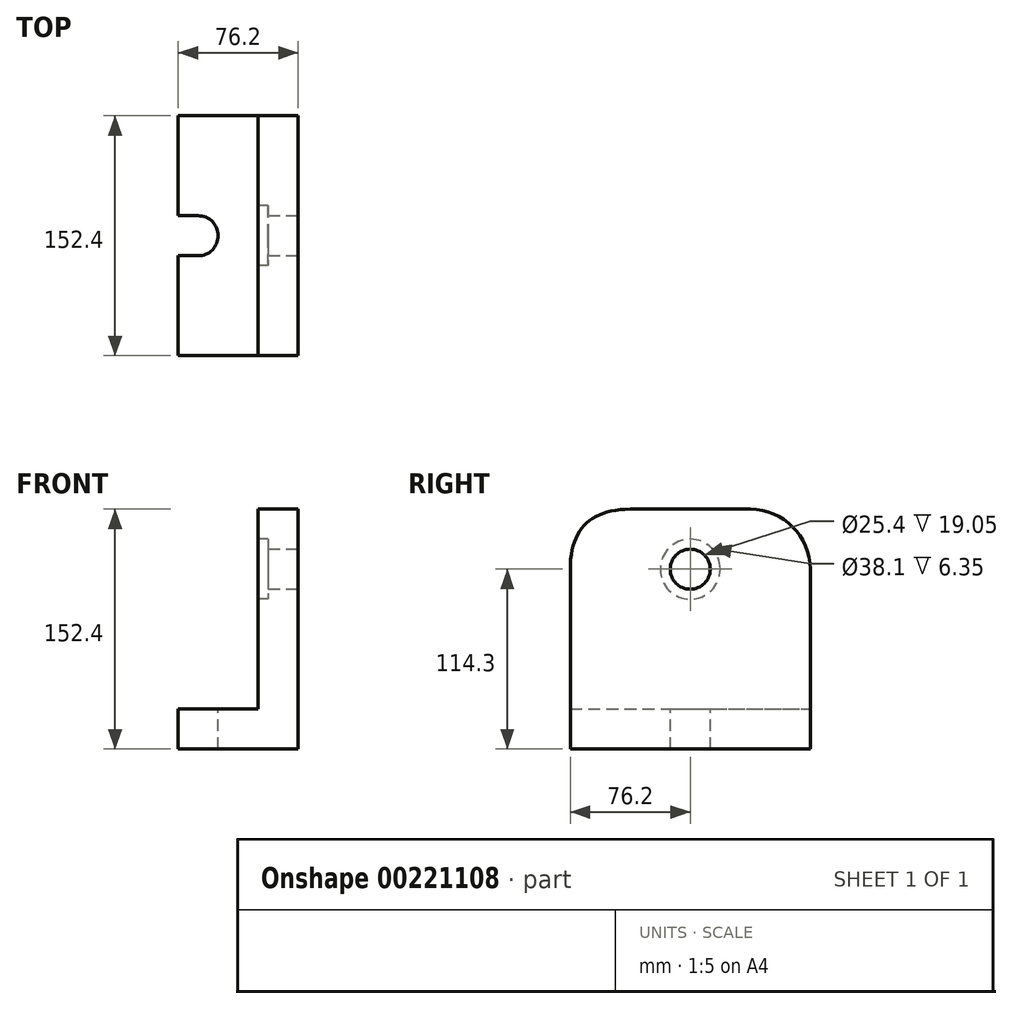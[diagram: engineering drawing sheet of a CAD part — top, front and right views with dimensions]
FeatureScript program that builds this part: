
annotation { "Feature Type Name" : "Feature", "Feature Type Description" : "" }
export const myFeature = defineFeature(function(context is Context, id is Id, definition is map)
    precondition{}
    {
        {
            var Q0;
            Q0=qCreatedBy(makeId("Front.planeOp"),FACE);
            var sketch = newSketch(context, id + "F0", { "sketchPlane" : qUnion([Q0])});
            skLineSegment(sketch, "E0", {"start": v(0, 0) * mm, "end": v(-76.2, 0) * mm});
            skLineSegment(sketch, "E1", {"start": v(0, 0) * mm, "end": v(0, 152.4) * mm});
            skLineSegment(sketch, "E2", {"start": v(-76.2, 0) * mm, "end": v(-76.2, 25.4) * mm});
            skLineSegment(sketch, "E3", {"start": v(-76.2, 25.4) * mm, "end": v(-25.4, 25.4) * mm});
            skLineSegment(sketch, "E4", {"start": v(-25.4, 25.4) * mm, "end": v(-25.4, 152.4) * mm});
            skLineSegment(sketch, "E5", {"start": v(-25.4, 152.4) * mm, "end": v(0, 152.4) * mm});
            skSolve(sketch);
        }
        {
            var Q0;
            Q0=makeQuery(id+"F0.imprint","IMPRINT",FACE,{"disambiguationData":[TD([[makeQuery(id+"F0.imprint","IMPRINT",EDGE,{"derivedFrom":sQuery(id+"F0.wireOp",EDGE,"E0")}),-1.0]])]});
            extrude(context, id + "F1", {"entities" : qUnion([Q0]), "endBound" : BoundingType.SYMMETRIC, "depth" : 152.4 * mm});
        }
        {
            var Q0;
            Q0=makeQuery(id+"F1.opExtrude","SWEPT_FACE",FACE,{"disambiguationData":[OSD([sQuery(id+"F0.wireOp",EDGE,"E1")])]});
            var sketch = newSketch(context, id + "F2", { "sketchPlane" : qUnion([Q0])});
            skCircle(sketch, "E6", {"center": v(0, 114.3) * mm, "radius": 12.7 * mm});
            skPoint(sketch, "E6.centerSnap0", {"position": v(0, 152.4) * mm});
            skSolve(sketch);
        }
        {
            var Q0;
            Q0=makeQuery(id+"F2.imprint","IMPRINT",FACE,{"disambiguationData":[TD([[makeQuery(id+"F2.imprint","IMPRINT",EDGE,{"derivedFrom":sQuery(id+"F2.wireOp",EDGE,"E6")}),1.0]])]});
            extrude(context, id + "F3", {"entities" : qUnion([Q0]), "operationType" : NewBodyOperationType.REMOVE, "oppositeDirection" : true, "depth" : 38.1 * mm});
        }
        {
            var Q0;
            Q0=makeQuery(id+"F1.opExtrude","SWEPT_FACE",FACE,{"disambiguationData":[OSD([sQuery(id+"F0.wireOp",EDGE,"E3")])]});
            var sketch = newSketch(context, id + "F4", { "sketchPlane" : qUnion([Q0])});
            skLineSegment(sketch, "E7", {"start": v(-76.2, 12.7) * mm, "end": v(-63.5, 12.7) * mm});
            skLineSegment(sketch, "E8", {"start": v(-76.2, -12.7) * mm, "end": v(-63.5, -12.7) * mm});
            skArc(sketch, "E9", {"start": v(-63.5, -12.7) * mm, "mid": v(-50.8, 0) * mm, "end": v(-63.5, 12.7) * mm});
            skSolve(sketch);
        }
        {
            var Q0;
            {var subQ0=sQuery(id+"F4.wireOp",EDGE,"E7");Q0=makeQuery(id+"F4.imprint","IMPRINT",FACE,{"disambiguationData":[TD([[makeQuery(id+"F4.imprint","IMPRINT",EDGE,{"derivedFrom":subQ0}),-1.0]])]});}
            extrude(context, id + "F5", {"entities" : qUnion([Q0]), "operationType" : NewBodyOperationType.REMOVE, "oppositeDirection" : true, "depth" : 25.4 * mm});
        }
        {
            var Q0;
            Q0=makeQuery(id+"F1.opExtrude","CAP_EDGE",EDGE,{"disambiguationData":[OSD([sQuery(id+"F0.wireOp",EDGE,"E5")])],"isStart":false});
            fillet(context, id + "F6", {"entities" : qUnion([Q0]), "radius" : 38.1 * mm, "tangentPropagation" : true, "rho" : 0.5, "crossSection" : FilletCrossSection.CONIC, "allowEdgeOverflow" : false});
        }
        {
            var Q0;
            Q0=makeQuery(id+"F1.opExtrude","CAP_EDGE",EDGE,{"disambiguationData":[OSD([sQuery(id+"F0.wireOp",EDGE,"E5")])],"isStart":true});
            fillet(context, id + "F7", {"entities" : qUnion([Q0]), "radius" : 38.1 * mm, "tangentPropagation" : true, "allowEdgeOverflow" : false});
        }
        {
            var Q0;
            Q0=makeQuery(id+"F1.opExtrude","SWEPT_FACE",FACE,{"disambiguationData":[OSD([sQuery(id+"F0.wireOp",EDGE,"E4")])]});
            var sketch = newSketch(context, id + "F8", { "sketchPlane" : qUnion([Q0])});
            skCircle(sketch, "E10", {"center": v(0, 114.3) * mm, "radius": 19.05 * mm});
            skSolve(sketch);
        }
        {
            var Q0;
            Q0=makeQuery(id+"F8.imprint","IMPRINT",FACE,{"disambiguationData":[TD([[makeQuery(id+"F8.imprint","IMPRINT",EDGE,{"derivedFrom":sQuery(id+"F8.wireOp",EDGE,"E10")}),1.0]])]});
            var Q1;
            Q1=sQuery(id+"F8.wireOp",EDGE,"E10");
            extrude(context, id + "F9", {"entities" : qUnion([Q0]), "operationType" : NewBodyOperationType.REMOVE, "surfaceEntities" : qUnion([Q1]), "oppositeDirection" : true, "depth" : 6.35 * mm});
        }
    });
